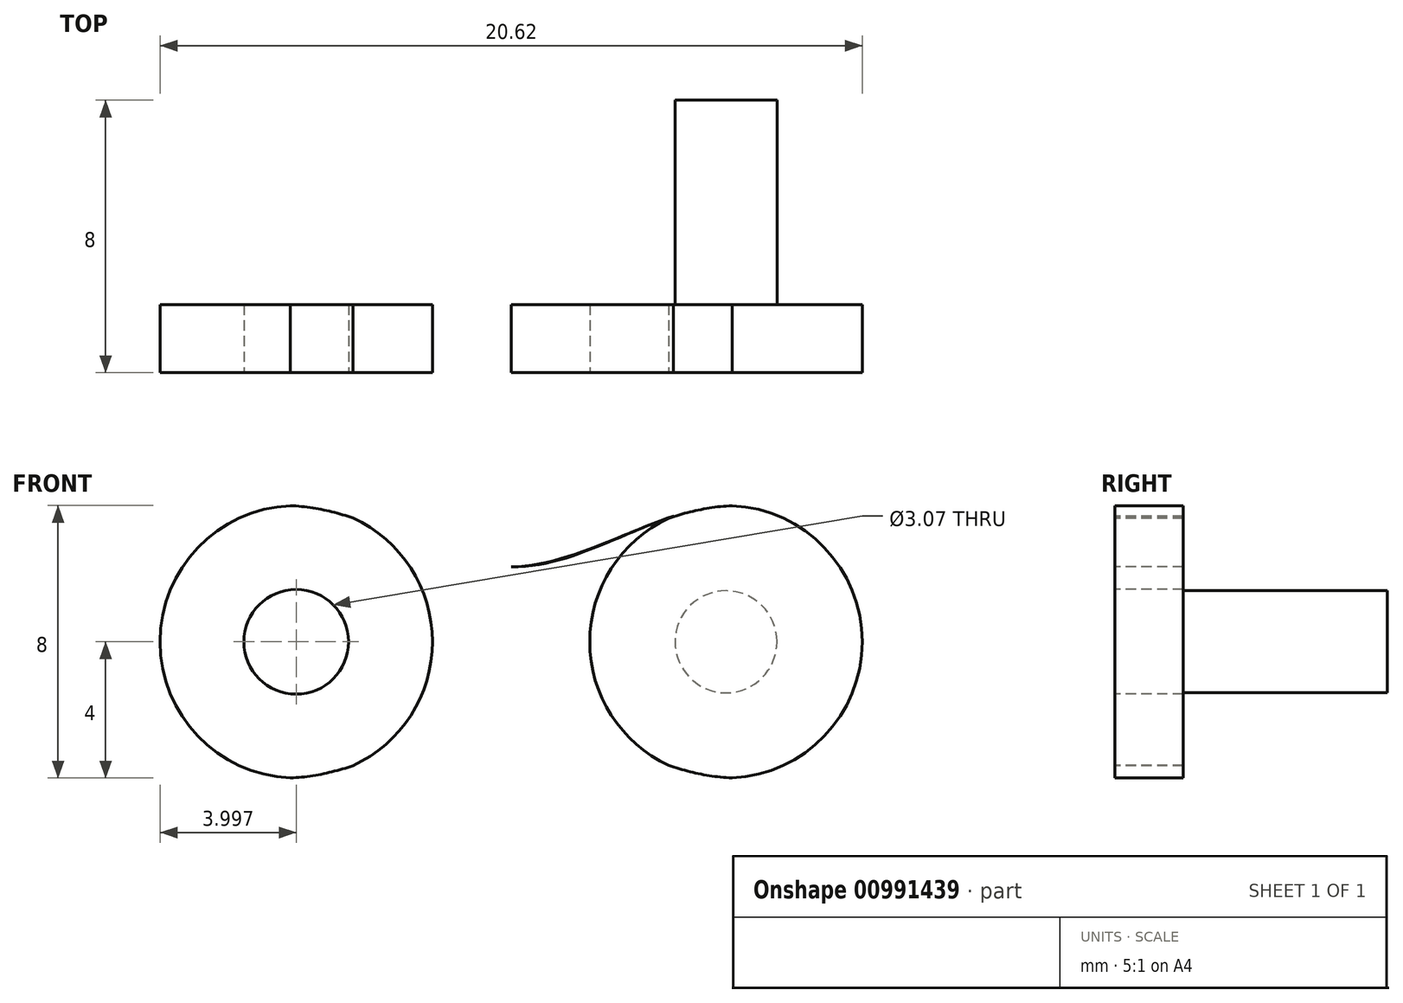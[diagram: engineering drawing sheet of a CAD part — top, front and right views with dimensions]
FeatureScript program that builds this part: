
annotation { "Feature Type Name" : "Feature", "Feature Type Description" : "" }
export const myFeature = defineFeature(function(context is Context, id is Id, definition is map)
    precondition{}
    {
        {
            var Q0;
            Q0=qCreatedBy(makeId("Front.planeOp"),FACE);
            var sketch = newSketch(context, id + "F0", { "sketchPlane" : qUnion([Q0])});
            skCircle(sketch, "E0", {"center": v(-6.31, 0) * mm, "radius": 1.54 * mm});
            skCircle(sketch, "E1", {"center": v(6.3, 0) * mm, "radius": 1.5 * mm});
            skCircle(sketch, "E2", {"center": v(6.3, 0) * mm, "radius": 4 * mm});
            skCircle(sketch, "E3", {"center": v(-6.31, 0) * mm, "radius": 4 * mm});
            skFitSpline(sketch, "E4", {"points": [v(-6.49, 4) * mm, v(0, 2.2) * mm, v(6.3, 4) * mm], "startDerivative": vector(14.5, -0.58) * mm, "endDerivative": vector(10.86, 0.01) * mm});
            skFitSpline(sketch, "E5.MirrorCS", {"points": [v(6.49, 4) * mm, v(0, 2.2) * mm, v(-6.3, 4) * mm], "startDerivative": vector(-14.5, -0.58) * mm, "endDerivative": vector(-10.86, 0.01) * mm});
            skFitSpline(sketch, "E6.MirrorCS", {"points": [v(-6.49, -4) * mm, v(0, -2.2) * mm, v(6.3, -4) * mm], "startDerivative": vector(14.5, 0.58) * mm, "endDerivative": vector(10.86, -0.01) * mm});
            skFitSpline(sketch, "E7.MirrorCS", {"points": [v(6.49, -4) * mm, v(0, -2.2) * mm, v(-6.3, -4) * mm], "startDerivative": vector(-14.5, 0.58) * mm, "endDerivative": vector(-10.86, -0.01) * mm});
            skLineSegment(sketch, "E8", {"start": v(6.3, 0) * mm, "end": v(4.81, 0.09) * mm});
            skSolve(sketch);
        }
        {
            var Q0;
            Q0=makeQuery(id+"F0.imprint","IMPRINT",FACE,{"disambiguationData":[TD([[makeQuery(id+"F0.imprint","IMPRINT",EDGE,{"derivedFrom":sQuery(id+"F0.wireOp",EDGE,"E0")}),-1.0]])]});
            var Q1;
            {var subQ1=sQuery(id+"F0.wireOp",EDGE,"E4");var subQ5=sQuery(id+"F0.wireOp",EDGE,"E2");var subQ6=makeQuery(id+"F0.imprint","INTERSECT",VERTEX,{"disambiguationData":[OD(1.0)],"derivedFrom":[subQ5,subQ1]});Q1=makeQuery(id+"F0.imprint","IMPRINT",FACE,{"disambiguationData":[TD([[makeQuery(id+"F0.imprint","IMPRINT",EDGE,{"disambiguationData":[TD([[subQ6,-1.0]])],"derivedFrom":subQ5}),-1.0]])]});}
            var Q2;
            Q2=makeQuery(id+"F0.imprint","IMPRINT",FACE,{"disambiguationData":[TD([[makeQuery(id+"F0.imprint","IMPRINT",EDGE,{"derivedFrom":sQuery(id+"F0.wireOp",EDGE,"E1")}),-1.0]])]});
            extrude(context, id + "F1", {"entities" : qUnion([Q0, Q1, Q2]), "depth" : -2 * mm, "offsetDistance" : 25.4 * mm});
        }
        {
            var Q0;
            Q0=sQuery(id+"F0.wireOp",EDGE,"E8");
            extrude(context, id + "F2", {"bodyType" : ExtendedToolBodyType.SURFACE, "surfaceEntities" : qUnion([Q0]), "depth" : -8 * mm, "offsetDistance" : 25.4 * mm});
        }
        {
            var Q0;
            Q0=makeQuery(id+"F2.opExtrude","SWEPT_FACE",FACE,{"disambiguationData":[OSD([sQuery(id+"F0.wireOp",EDGE,"E8")])]});
            var Q1;
            Q1=makeQuery(id+"F2.opExtrude","SWEPT_EDGE",EDGE,{"disambiguationData":[OSD([sQuery(id+"F0.wireOp",VERTEX,"E8.start")])]});
            revolve(context, id + "F3", {"operationType" : NewBodyOperationType.ADD, "surfaceOperationType" : NewSurfaceOperationType.NEW, "entities" : qUnion([Q0]), "axis" : qUnion([Q1]), "revolveType" : RevolveType.FULL});
        }
    });
